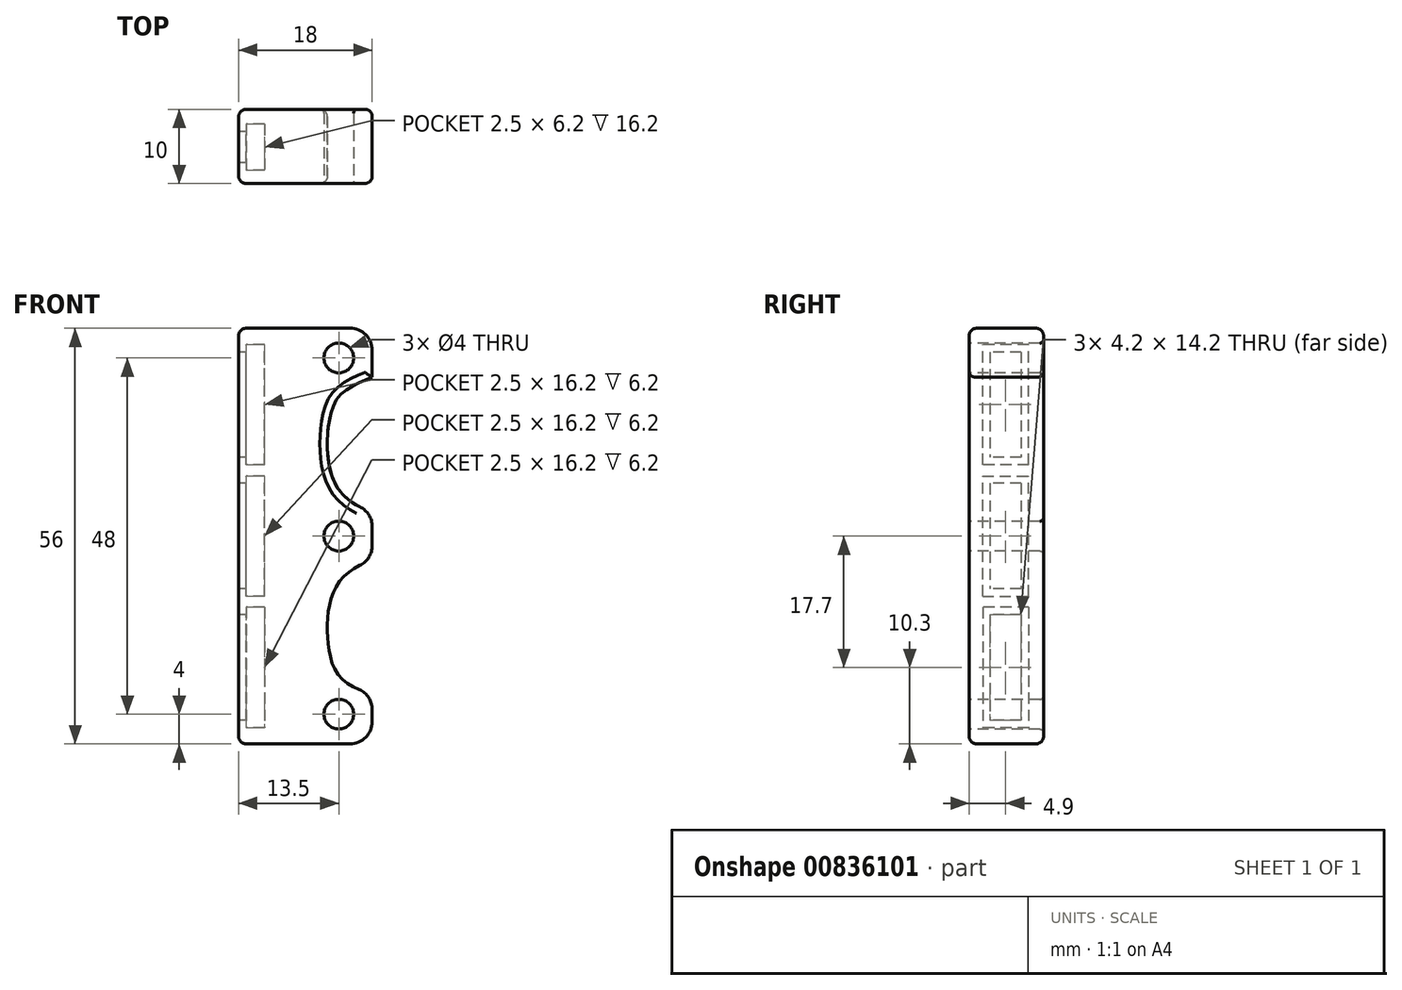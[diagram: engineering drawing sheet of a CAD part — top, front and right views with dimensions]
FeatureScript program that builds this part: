
annotation { "Feature Type Name" : "Feature", "Feature Type Description" : "" }
export const myFeature = defineFeature(function(context is Context, id is Id, definition is map)
    precondition{}
    {
        {
            var Q0;
            Q0=qCreatedBy(makeId("Front.planeOp"),FACE);
            var sketch = newSketch(context, id + "F0", { "sketchPlane" : qUnion([Q0])});
            skLineSegment(sketch, "E0.bottom", {"start": v(0, 28) * mm, "end": v(18, 28) * mm});
            skLineSegment(sketch, "E0.top", {"start": v(0, -28) * mm, "end": v(18, -28) * mm});
            skLineSegment(sketch, "E0.left", {"start": v(0, 28) * mm, "end": v(0, -28) * mm});
            skLineSegment(sketch, "E0.right", {"start": v(18, 28) * mm, "end": v(18, -28) * mm});
            skSolve(sketch);
        }
        {
            var Q0;
            Q0 = qSketchRegion(id + "F0", true);
            extrude(context, id + "F1", {"entities" : qUnion([Q0]), "depth" : 10 * mm, "offsetDistance" : 25 * mm});
        }
        {
            var Q0;
            Q0=makeQuery(id+"F1.opExtrude","CAP_FACE",FACE,{"disambiguationData":[OSD([sQuery(id+"F0.wireOp",EDGE,"E0.bottom"),sQuery(id+"F0.wireOp",EDGE,"E0.top"),sQuery(id+"F0.wireOp",EDGE,"E0.left"),sQuery(id+"F0.wireOp",EDGE,"E0.right")])],"isStart":false});
            var sketch = newSketch(context, id + "F2", { "sketchPlane" : qUnion([Q0])});
            skCircle(sketch, "E1", {"center": v(13.5, 0) * mm, "radius": 2 * mm});
            skCircle(sketch, "E2", {"center": v(13.5, -24) * mm, "radius": 2 * mm});
            skCircle(sketch, "E3", {"center": v(13.5, 24) * mm, "radius": 2 * mm});
            skLineSegment(sketch, "E4", {"start": v(13.5, 24) * mm, "end": v(13.5, -24) * mm, "construction": true});
            skSolve(sketch);
        }
        {
            var Q0;
            Q0 = qSketchRegion(id + "F2", true);
            extrude(context, id + "F3", {"entities" : qUnion([Q0]), "operationType" : NewBodyOperationType.REMOVE, "oppositeDirection" : true, "depth" : 25 * mm, "offsetDistance" : 25 * mm});
        }
        {
            var Q0;
            Q0=makeQuery(id+"F1.opExtrude","SWEPT_EDGE",EDGE,{"disambiguationData":[OSD([sQuery(id+"F0.wireOp",EDGE,"E0.bottom"),sQuery(id+"F0.wireOp",EDGE,"E0.right")])]});
            var Q1;
            Q1=makeQuery(id+"F1.opExtrude","SWEPT_EDGE",EDGE,{"disambiguationData":[OSD([sQuery(id+"F0.wireOp",EDGE,"E0.top"),sQuery(id+"F0.wireOp",EDGE,"E0.right")])]});
            fillet(context, id + "F4", {"entities" : qUnion([Q0, Q1]), "radius" : 3 * mm, "tangentPropagation" : true, "allowEdgeOverflow" : false});
        }
        {
            var Q0;
            Q0=makeQuery(id+"F1.opExtrude","CAP_FACE",FACE,{"disambiguationData":[OSD([sQuery(id+"F0.wireOp",EDGE,"E0.bottom"),sQuery(id+"F0.wireOp",EDGE,"E0.top"),sQuery(id+"F0.wireOp",EDGE,"E0.left"),sQuery(id+"F0.wireOp",EDGE,"E0.right")])],"isStart":false});
            var sketch = newSketch(context, id + "F5", { "sketchPlane" : qUnion([Q0])});
            skFitSpline(sketch, "E5", {"points": [v(18, 21.38) * mm, v(12.51, 16.82) * mm, v(12.56, 8.11) * mm, v(18, 3.24) * mm], "startDerivative": vector(-35.06, -13.2) * mm, "endDerivative": vector(28.08, -10.18) * mm});
            skFitSpline(sketch, "E6.MirrorCS", {"points": [v(18, -21.38) * mm, v(12.51, -16.82) * mm, v(12.56, -8.11) * mm, v(18, -3.24) * mm], "startDerivative": vector(-35.06, 13.2) * mm, "endDerivative": vector(28.08, 10.18) * mm});
            skLineSegment(sketch, "E7", {"start": v(18, 21.38) * mm, "end": v(18, 3.24) * mm});
            skLineSegment(sketch, "E8", {"start": v(18, -3.24) * mm, "end": v(18, -21.38) * mm});
            skSolve(sketch);
        }
        {
            var Q0;
            Q0 = qSketchRegion(id + "F5", true);
            extrude(context, id + "F6", {"entities" : qUnion([Q0]), "operationType" : NewBodyOperationType.REMOVE, "oppositeDirection" : true, "depth" : 25 * mm, "offsetDistance" : 25 * mm});
        }
        {
            var Q0;
            {var subQ0=sQuery(id+"F5.wireOp",EDGE,"E7");var subQ1=sQuery(id+"F5.wireOp",EDGE,"E5");var subQ2=sQuery(id+"F0.wireOp",EDGE,"E0.right");Q0=makeQuery(id+"F6.boolean.opBoolean","COPY",EDGE,{"derivedFrom":makeQuery(id+"F6.opExtrude","SWEPT_EDGE",EDGE,{"disambiguationData":[OSD([subQ2,subQ1,subQ0]),TDD([makeQuery(id+"F5.imprint","INTERSECT",VERTEX,{"disambiguationData":[OD(0.0)],"derivedFrom":[makeQuery(id+"F1.opExtrude","CAP_EDGE",EDGE,{"disambiguationData":[OSD([subQ2])],"isStart":false}),subQ1,subQ0]})])]})});}
            var Q1;
            {var subQ0=sQuery(id+"F5.wireOp",EDGE,"E8");var subQ1=sQuery(id+"F5.wireOp",EDGE,"E6.MirrorCS");var subQ2=sQuery(id+"F0.wireOp",EDGE,"E0.right");Q1=makeQuery(id+"F6.boolean.opBoolean","COPY",EDGE,{"derivedFrom":makeQuery(id+"F6.opExtrude","SWEPT_EDGE",EDGE,{"disambiguationData":[OSD([subQ2,subQ1,subQ0]),TDD([makeQuery(id+"F5.imprint","INTERSECT",VERTEX,{"disambiguationData":[OD(1.0)],"derivedFrom":[makeQuery(id+"F1.opExtrude","CAP_EDGE",EDGE,{"disambiguationData":[OSD([subQ2])],"isStart":false}),subQ1,subQ0]})])]})});}
            var Q2;
            {var subQ0=sQuery(id+"F5.wireOp",EDGE,"E7");var subQ1=sQuery(id+"F5.wireOp",EDGE,"E5");var subQ2=sQuery(id+"F0.wireOp",EDGE,"E0.right");Q2=makeQuery(id+"F6.boolean.opBoolean","COPY",EDGE,{"derivedFrom":makeQuery(id+"F6.opExtrude","SWEPT_EDGE",EDGE,{"disambiguationData":[OSD([subQ2,subQ1,subQ0]),TDD([makeQuery(id+"F5.imprint","INTERSECT",VERTEX,{"disambiguationData":[OD(1.0)],"derivedFrom":[makeQuery(id+"F1.opExtrude","CAP_EDGE",EDGE,{"disambiguationData":[OSD([subQ2])],"isStart":false}),subQ1,subQ0]})])]})});}
            var Q3;
            {var subQ0=sQuery(id+"F5.wireOp",EDGE,"E8");var subQ1=sQuery(id+"F5.wireOp",EDGE,"E6.MirrorCS");var subQ2=sQuery(id+"F0.wireOp",EDGE,"E0.right");Q3=makeQuery(id+"F6.boolean.opBoolean","COPY",EDGE,{"derivedFrom":makeQuery(id+"F6.opExtrude","SWEPT_EDGE",EDGE,{"disambiguationData":[OSD([subQ2,subQ1,subQ0]),TDD([makeQuery(id+"F5.imprint","INTERSECT",VERTEX,{"disambiguationData":[OD(0.0)],"derivedFrom":[makeQuery(id+"F1.opExtrude","CAP_EDGE",EDGE,{"disambiguationData":[OSD([subQ2])],"isStart":false}),subQ1,subQ0]})])]})});}
            fillet(context, id + "F7", {"entities" : qUnion([Q0, Q1, Q2, Q3]), "radius" : 3 * mm, "tangentPropagation" : true, "allowEdgeOverflow" : false});
        }
        {
            var Q0;
            Q0=makeQuery(id+"F1.opExtrude","SWEPT_EDGE",EDGE,{"disambiguationData":[OSD([sQuery(id+"F0.wireOp",EDGE,"E0.top"),sQuery(id+"F0.wireOp",EDGE,"E0.left")])]});
            var Q1;
            Q1=makeQuery(id+"F1.opExtrude","SWEPT_EDGE",EDGE,{"disambiguationData":[OSD([sQuery(id+"F0.wireOp",EDGE,"E0.bottom"),sQuery(id+"F0.wireOp",EDGE,"E0.left")])]});
            fillet(context, id + "F8", {"entities" : qUnion([Q0, Q1]), "radius" : 1 * mm, "tangentPropagation" : true, "allowEdgeOverflow" : false});
        }
        {
            var Q0;
            Q0=makeQuery(id+"F1.opExtrude","SWEPT_FACE",FACE,{"disambiguationData":[OSD([sQuery(id+"F0.wireOp",EDGE,"E0.left")])]});
            cPlane(context, id + "F9", {"entities" : qUnion([Q0]), "cplaneType" : CPlaneType.OFFSET, "offset" : 1 * mm, "oppositeDirection" : true, "width" : 150 * mm, "height" : 150 * mm});
        }
        {
            var Q0;
            Q0=qCreatedBy(id+"F9.planeOp",FACE);
            var sketch = newSketch(context, id + "F10", { "sketchPlane" : qUnion([Q0])});
            skLineSegment(sketch, "E9.bottom", {"start": v(2, -9.6) * mm, "end": v(8.2, -9.6) * mm});
            skLineSegment(sketch, "E9.top", {"start": v(2, -25.8) * mm, "end": v(8.2, -25.8) * mm});
            skLineSegment(sketch, "E9.left", {"start": v(2, -9.6) * mm, "end": v(2, -25.8) * mm});
            skLineSegment(sketch, "E9.right", {"start": v(8.2, -9.6) * mm, "end": v(8.2, -25.8) * mm});
            skLineSegment(sketch, "E10.bottom", {"start": v(8.2, -8.1) * mm, "end": v(2, -8.1) * mm});
            skLineSegment(sketch, "E10.top", {"start": v(8.2, 8.1) * mm, "end": v(2, 8.1) * mm});
            skLineSegment(sketch, "E10.left", {"start": v(8.2, -8.1) * mm, "end": v(8.2, 8.1) * mm});
            skLineSegment(sketch, "E10.right", {"start": v(2, -8.1) * mm, "end": v(2, 8.1) * mm});
            skLineSegment(sketch, "E11.MirrorCS", {"start": v(2, 9.6) * mm, "end": v(8.2, 9.6) * mm});
            skLineSegment(sketch, "E12.MirrorCS", {"start": v(2, 9.6) * mm, "end": v(2, 25.8) * mm});
            skLineSegment(sketch, "E13.MirrorCS", {"start": v(2, 25.8) * mm, "end": v(8.2, 25.8) * mm});
            skLineSegment(sketch, "E14.MirrorCS", {"start": v(8.2, 9.6) * mm, "end": v(8.2, 25.8) * mm});
            skSolve(sketch);
        }
        {
            var Q0;
            Q0 = qSketchRegion(id + "F10", true);
            extrude(context, id + "F11", {"entities" : qUnion([Q0]), "operationType" : NewBodyOperationType.REMOVE, "oppositeDirection" : true, "depth" : 2.5 * mm, "offsetDistance" : 25 * mm});
        }
        {
            var Q0;
            Q0=makeQuery(id+"F1.opExtrude","CAP_EDGE",EDGE,{"disambiguationData":[OSD([sQuery(id+"F0.wireOp",EDGE,"E0.bottom")])],"isStart":false});
            var Q1;
            Q1=makeQuery(id+"F1.opExtrude","CAP_EDGE",EDGE,{"disambiguationData":[OSD([sQuery(id+"F0.wireOp",EDGE,"E0.left")])],"isStart":true});
            fillet(context, id + "F12", {"entities" : qUnion([Q0, Q1]), "radius" : 1 * mm, "tangentPropagation" : true, "allowEdgeOverflow" : false});
        }
        {
            var Q0;
            Q0=makeQuery(id+"F3.boolean.opBoolean","COPY",EDGE,{"derivedFrom":makeQuery(id+"F3.opExtrude","CAP_EDGE",EDGE,{"disambiguationData":[OSD([sQuery(id+"F2.wireOp",EDGE,"E2")])],"isStart":true})});
            var Q1;
            Q1=makeQuery(id+"F3.boolean.opBoolean","COPY",EDGE,{"derivedFrom":makeQuery(id+"F3.opExtrude","CAP_EDGE",EDGE,{"disambiguationData":[OSD([sQuery(id+"F2.wireOp",EDGE,"E1")])],"isStart":true})});
            var Q2;
            Q2=makeQuery(id+"F3.boolean.opBoolean","COPY",EDGE,{"derivedFrom":makeQuery(id+"F3.opExtrude","CAP_EDGE",EDGE,{"disambiguationData":[OSD([sQuery(id+"F2.wireOp",EDGE,"E3")])],"isStart":true})});
            var Q3;
            Q3=makeQuery(id+"F3.boolean.opBoolean","INTERSECT",EDGE,{"derivedFrom":[makeQuery(id+"F1.opExtrude","CAP_FACE",FACE,{"disambiguationData":[OSD([sQuery(id+"F0.wireOp",EDGE,"E0.bottom"),sQuery(id+"F0.wireOp",EDGE,"E0.top"),sQuery(id+"F0.wireOp",EDGE,"E0.left"),sQuery(id+"F0.wireOp",EDGE,"E0.right")])],"isStart":true}),makeQuery(id+"F3.opExtrude","SWEPT_FACE",FACE,{"disambiguationData":[OSD([sQuery(id+"F2.wireOp",EDGE,"E3")])]})]});
            var Q4;
            Q4=makeQuery(id+"F3.boolean.opBoolean","INTERSECT",EDGE,{"derivedFrom":[makeQuery(id+"F1.opExtrude","CAP_FACE",FACE,{"disambiguationData":[OSD([sQuery(id+"F0.wireOp",EDGE,"E0.bottom"),sQuery(id+"F0.wireOp",EDGE,"E0.top"),sQuery(id+"F0.wireOp",EDGE,"E0.left"),sQuery(id+"F0.wireOp",EDGE,"E0.right")])],"isStart":true}),makeQuery(id+"F3.opExtrude","SWEPT_FACE",FACE,{"disambiguationData":[OSD([sQuery(id+"F2.wireOp",EDGE,"E1")])]})]});
            var Q5;
            Q5=makeQuery(id+"F3.boolean.opBoolean","INTERSECT",EDGE,{"derivedFrom":[makeQuery(id+"F1.opExtrude","CAP_FACE",FACE,{"disambiguationData":[OSD([sQuery(id+"F0.wireOp",EDGE,"E0.bottom"),sQuery(id+"F0.wireOp",EDGE,"E0.top"),sQuery(id+"F0.wireOp",EDGE,"E0.left"),sQuery(id+"F0.wireOp",EDGE,"E0.right")])],"isStart":true}),makeQuery(id+"F3.opExtrude","SWEPT_FACE",FACE,{"disambiguationData":[OSD([sQuery(id+"F2.wireOp",EDGE,"E2")])]})]});
            fillet(context, id + "F13", {"entities" : qUnion([Q0, Q1, Q2, Q3, Q4, Q5]), "radius" : 0.5 * mm, "tangentPropagation" : true, "allowEdgeOverflow" : false});
        }
        {
            var Q0;
            Q0=makeQuery(id+"F1.opExtrude","SWEPT_FACE",FACE,{"disambiguationData":[OSD([sQuery(id+"F0.wireOp",EDGE,"E0.left")])]});
            var sketch = newSketch(context, id + "F14", { "sketchPlane" : qUnion([Q0])});
            skLineSegment(sketch, "E15.bottom", {"start": v(3, 24.8) * mm, "end": v(7.2, 24.8) * mm});
            skLineSegment(sketch, "E15.top", {"start": v(3, 10.6) * mm, "end": v(7.2, 10.6) * mm});
            skLineSegment(sketch, "E15.left", {"start": v(3, 24.8) * mm, "end": v(3, 10.6) * mm});
            skLineSegment(sketch, "E15.right", {"start": v(7.2, 24.8) * mm, "end": v(7.2, 10.6) * mm});
            skLineSegment(sketch, "E16.bottom", {"start": v(3, 7.1) * mm, "end": v(7.2, 7.1) * mm});
            skLineSegment(sketch, "E16.top", {"start": v(3, -7.1) * mm, "end": v(7.2, -7.1) * mm});
            skLineSegment(sketch, "E16.left", {"start": v(3, 7.1) * mm, "end": v(3, -7.1) * mm});
            skLineSegment(sketch, "E16.right", {"start": v(7.2, 7.1) * mm, "end": v(7.2, -7.1) * mm});
            skLineSegment(sketch, "E17.bottom", {"start": v(3, -10.6) * mm, "end": v(7.2, -10.6) * mm});
            skLineSegment(sketch, "E17.top", {"start": v(3, -24.8) * mm, "end": v(7.2, -24.8) * mm});
            skLineSegment(sketch, "E17.left", {"start": v(3, -10.6) * mm, "end": v(3, -24.8) * mm});
            skLineSegment(sketch, "E17.right", {"start": v(7.2, -10.6) * mm, "end": v(7.2, -24.8) * mm});
            skSolve(sketch);
        }
        {
            var Q0;
            Q0 = qSketchRegion(id + "F14", true);
            extrude(context, id + "F15", {"entities" : qUnion([Q0]), "operationType" : NewBodyOperationType.REMOVE, "endBound" : BoundingType.UP_TO_NEXT, "oppositeDirection" : true, "depth" : 25 * mm, "offsetDistance" : 25 * mm});
        }
    });
